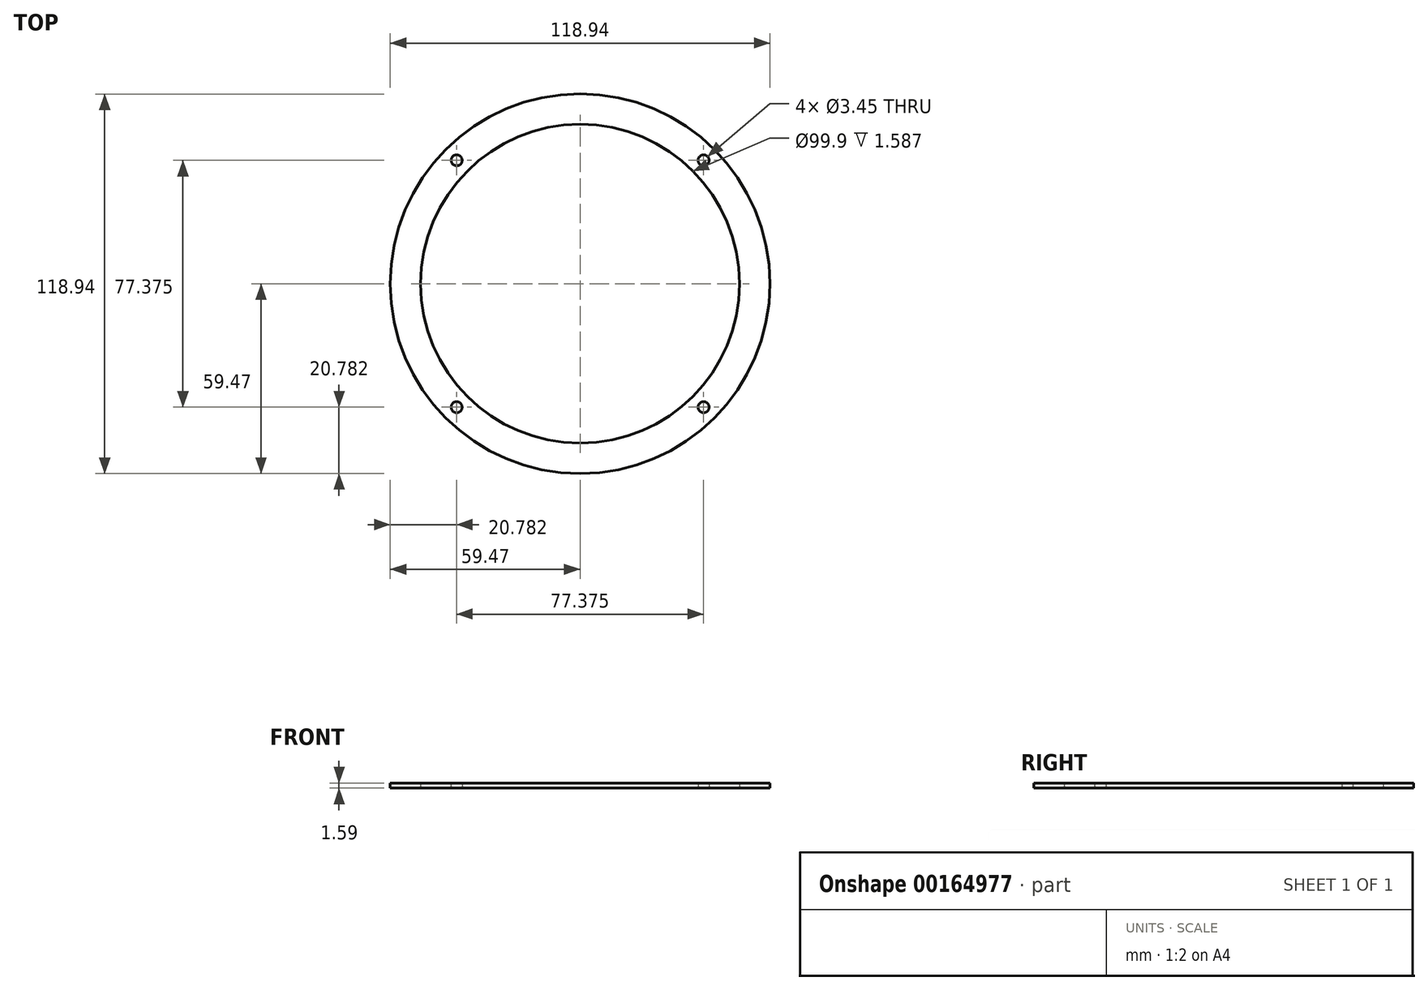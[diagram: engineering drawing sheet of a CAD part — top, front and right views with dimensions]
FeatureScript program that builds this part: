
annotation { "Feature Type Name" : "Feature", "Feature Type Description" : "" }
export const myFeature = defineFeature(function(context is Context, id is Id, definition is map)
    precondition{}
    {
        {
            var Q0;
            Q0=qCreatedBy(makeId("Top.planeOp"),FACE);
            var sketch = newSketch(context, id + "F0", { "sketchPlane" : qUnion([Q0])});
            skCircle(sketch, "E0", {"center": v(0, 0) * mm, "radius": 59.47 * mm});
            skCircle(sketch, "E1", {"center": v(0, 0) * mm, "radius": 49.95 * mm});
            skLineSegment(sketch, "E2.bottom", {"start": v(-38.69, 38.69) * mm, "end": v(38.69, 38.69) * mm, "construction": true});
            skLineSegment(sketch, "E2.top", {"start": v(-38.69, -38.69) * mm, "end": v(38.69, -38.69) * mm, "construction": true});
            skLineSegment(sketch, "E2.left", {"start": v(-38.69, 38.69) * mm, "end": v(-38.69, -38.69) * mm, "construction": true});
            skLineSegment(sketch, "E2.right", {"start": v(38.69, 38.69) * mm, "end": v(38.69, -38.69) * mm, "construction": true});
            skCircle(sketch, "E3", {"center": v(-38.69, 38.69) * mm, "radius": 4.76 * mm, "construction": true});
            skCircle(sketch, "E4", {"center": v(-38.69, 38.69) * mm, "radius": 1.73 * mm});
            skCircle(sketch, "E5", {"center": v(38.69, 38.69) * mm, "radius": 1.73 * mm});
            skCircle(sketch, "E6", {"center": v(38.69, -38.69) * mm, "radius": 1.73 * mm});
            skCircle(sketch, "E7", {"center": v(-38.69, -38.69) * mm, "radius": 1.73 * mm});
            skSolve(sketch);
        }
        {
            var Q0;
            Q0=qSketchRegion(id+"F0",true);
            extrude(context, id + "F1", {"entities" : qUnion([Q0]), "depth" : 1.59 * mm});
        }
    });
